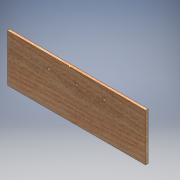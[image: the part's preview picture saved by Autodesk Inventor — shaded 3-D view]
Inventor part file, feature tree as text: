
AUTODESK INVENTOR PART (.ipt)
format: ipt  version: 2016 (Build 200138000, 138)  size: 178,176 bytes
history: native  units: mm
features: sketch x7, hole x4, extrude x2
ambient origin geometry x8: Origin, YZ Plane, XZ Plane, XY Plane, X Axis, Y Axis, Z Axis, Center Point
bodies: Solid1 (feature_tree)
feature tree (13):
  extrude  "Extrusion1"  Depth=120.0mm
  extrude  "Extrusion2"  Depth=31.0mm
  hole  "Hole1"  [1 undecoded]
  sketch  "Sketch4"  dims[d6=70.0mm d7=70.0mm]
  hole  "Hole2"  [1 undecoded]
  hole  "Hole3"  [1 undecoded]
  hole  "Hole4"  [1 undecoded]
  sketch  "Sketch1"  dims[d0=350.0mm d1=120.0mm]
  sketch  "Sketch2"  dims[d2=7.5mm d3=31.0mm]
  sketch  "Sketch3"  dims[d4=7.5mm d5=7.5mm]
  sketch  "Sketch5"  dims[d8=6.35mm d9=0.0mm d10=35.0mm]
  sketch  "Sketch6"  dims[d11=40.0mm d12=157.5mm]
  sketch  "Sketch7"  dims[d13=62.0mm d14=0.0mm d15=4.25mm d16=6.0mm d17=4.25mm d18=6.0mm d19=4.25mm d20=6.0mm d21=4.25mm d22=6.0mm d23=4.0mm d24=2.0mm d25=90.0deg d26=8.0mm d27=20.594885mm d28=20.0mm d29=3.0mm d30=3.0mm d31=6.0mm d32=6.0mm d33=6.0mm d34=6.0mm d35=3.0mm d36=6.0mm d37=4.0mm d38=2.0mm d39=90.0deg d40=2.0mm d41=20.594885mm d42=20.0mm d43=3.0mm d44=6.0mm d45=6.0mm d46=3.0mm d47=6.0mm d48=6.0mm d49=3.0mm d50=6.0mm d51=4.0mm d52=2.0mm d53=90.0deg d54=2.0mm d55=20.594885mm d56=3.0mm d57=3.0mm d58=3.0mm d59=6.0mm d60=4.0mm d61=2.0mm d62=90.0deg d63=2.0mm d64=20.594885mm]
note: 4 required parameter values undecoded (feature->parameter linkage not recoverable at this tier; creation-order binding heuristic only, values carry confidence <= 0.55)
